# Revit family: Cumberland-Revo-Lounge-1
name_source: partatom
category: Furniture
revit_build: Autodesk Revit 2014 (Build: 20140709_2115(x64)
units: mm (PartAtom-declared; Revit-internal decimal feet)

## types (4) — shared parameters
Arm Rest = CUM - Wood
Assembly Code = E2020200
Depth = 21 17/32"
Height = 29 9/16"
Keynote = 12500
Leg = CUM - Wood
Low Emitting Finish = Yes
Low Emitting Material = Yes
Manufacturer = Cumberland
Salvage or Reuse = Yes
Seat = CUM - Linen - Beige
Type Comments = Revo Lounge
URL = www.cumberlandfurniture.com
Width = 23 5/8"
Wood Back = CUM - Wood
zero-valued in all types: Percentage of Recycled Content

## per-type parameters (varying)
| type | ARM | Description | Model | Wd Back |
| Revo Lounge 2451 UPH | No | Revo Lounge, Armless | 2451 UPH | No |
| Revo Lounge 2450 UPH | Yes | Revo Lounge, Arm Chair | 2450 UPH | No |
| Revo Lounge 2450 UPH - Wood Back | Yes | Revo Lounge, Arm Chair Wood Back | 2450 UPH Wood Back | Yes |
| Revo Lounge 2451 UPH - Wood Back | No | Revo Lounge, Armless, Wood Back | 2451 UPH - Wood Back | Yes |

## geometry (parser evidence)
native form markers: Sweep x4
no freeform markers — native parametric forms only
